# Revit family: Column-Steel-TFB Tapered Flange Beam-Steel & Tube-350 AA
name_source: partatom
category: Structural Columns
revit_build: Autodesk Revit 2016 (Build: 20161004_0715(x64)
units: mm (PartAtom-declared; Revit-internal decimal feet)

## family parameters
Always export as geometry = No
Beam cutback in plan = From geometry
Cut with Voids When Loaded = No
Material for Model Behavior = Steel
OmniClass Number = 23.25.30.11.14.11
OmniClass Title = Columns
Section Shape = I-shape Sloped Flange
Shared = No
Show family pre-cut in plan views = Yes

## types (1)
- TFB125
    Assembly Code = B1010250
    CBICode = 3421
    CBIDescription = Light steel framing
    Centre Horizontal = 33 mm
    Centroid Horizontal = 32.5 mm
    Centroid Vertical = 62.5 mm
    Clear Web Height = 109.0 mm
    Description = Steel & Tube supplies a full range of hot rolled seismic and non seismic universal beams, columns, plate and channels. For more information please refer to the Design with Steel product catalogue on our website.
    Design Instruction = Design information should be cross referenced with the Steel & Tube Design with Steel Design Guide and NZS 3404: Part1: 2009
    Design Standard = NZS 3404: Part 1: 2009 including reference to the NZBC
    Elastic Modulus strong axis = 80300.0 mm³
    Elastic Modulus weak axis = 17200.0 mm³
    Flange Fillet = 4.0 mm
    Flange Thickness = 5.0 mm
    Flange Toe of Fillet = 10.5 mm
    Form Factor = 0
    Height = 125.0 mm
    Manufactured Standard = AS/NZS 3679.1: 2016
    Manufacturer = Steel & Tube
    ManufacturerName = Steel & Tube
    ManufacturerURL = http://www.steelandtube.co.nz
    MassPerUnitLength_ANZRS = 13.10 kg/m
    MaximumLength_ANZRS = 16500 mm  [stored 54.1339 ft]
    Model = 125TFB
    ModifiedIssue_ANZRS = 20160331.01 $
    Moment of Inertia strong axis = 4340000.00 mm4
    Moment of Inertia weak axis = 337000.00 mm4
    Nominal Weight = 13.10 kgf/m
    Perimeter = 0.47 m²/m
    Plastic Modulus strong axis = 69400.0 mm³
    Plastic Modulus weak axis = 10400.0 mm³
    Principal Axes Angle = 90.00°
    Section Area = 1670.0 mm²
    SectionAreaGross_ANZRS = 1670.0 mm²
    SectionAreaNet_ANZRS = 1670.0 mm²
    Shear Area strong axis = 1670.0 mm²
    Shear Area weak axis = 1670.0 mm²
    Tensile Strength = 0.0 MPa
    Torsional Modulus = 0.0 mm³
    Torsional Moment of Inertia = 40200.00 mm4
    URL = http://www.steelandtube.co.nz
    Uniclass2015Code = Pr_20_76_51_12
    Uniclass2015Title = Carbon steel beams, columns, channels and tees
    Uniclass2015Version = 2015
    Warping Constant = 1140000000.0 mm6
    Web Fillet = 8.0 mm
    Web Thickness = 5.0 mm
    Web Toe of Fillet = 22.0 mm
    Width = 65.0 mm
    X-Zex = 0.0 mm³
    Y-Zey = 0.0 mm³
    Yield Stress Flange = 0.0 MPa
    Yield Stress Web = 0.0 MPa

note: [stored X ft] marks values corroborated as IEEE doubles in the binary element streams (Revit-internal decimal feet)

## geometry (parser evidence)
native form markers: Sweep x5
no freeform markers — native parametric forms only
